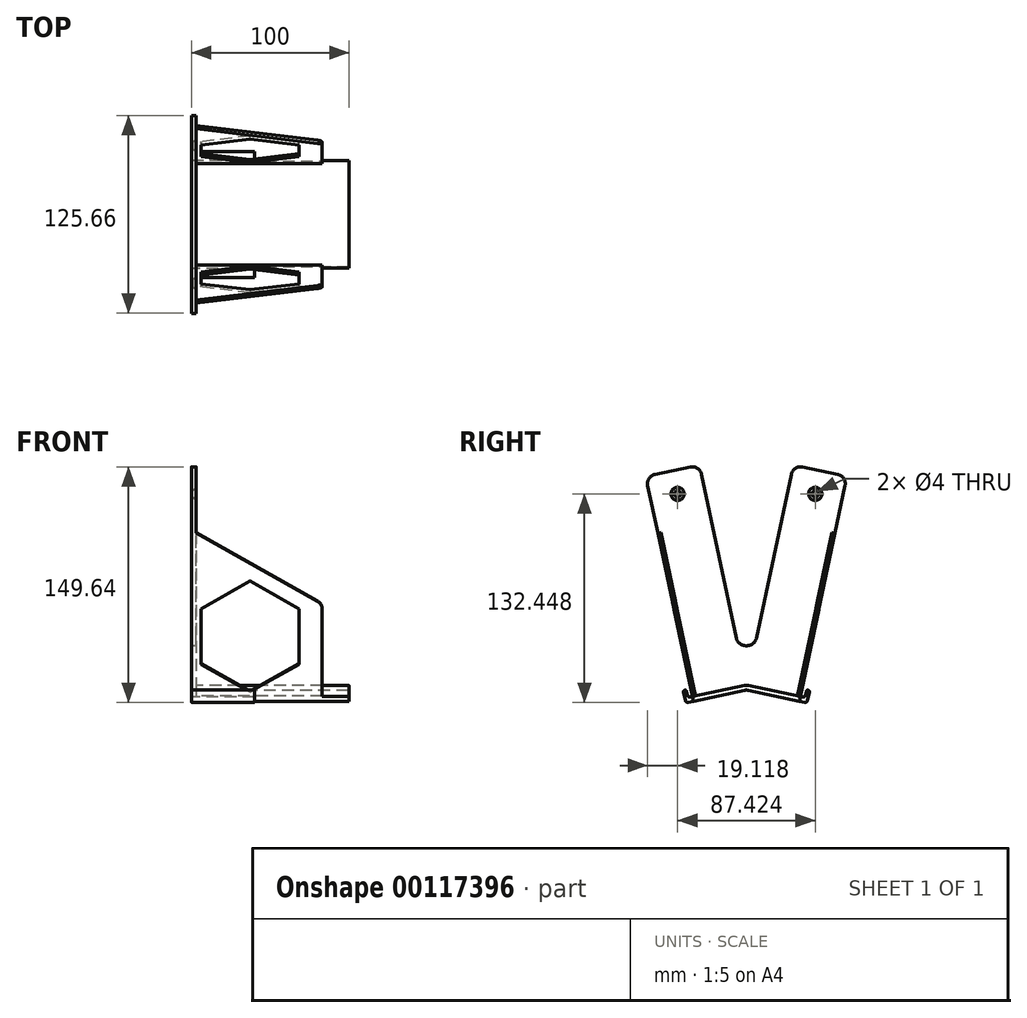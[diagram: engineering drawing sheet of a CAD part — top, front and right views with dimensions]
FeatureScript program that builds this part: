
annotation { "Feature Type Name" : "Feature", "Feature Type Description" : "" }
export const myFeature = defineFeature(function(context is Context, id is Id, definition is map)
    precondition{}
    {
        {
            var Q0;
            Q0=qCreatedBy(makeId("Right.planeOp"),FACE);
            var sketch = newSketch(context, id + "F0", { "sketchPlane" : qUnion([Q0])});
            skLineSegment(sketch, "E0", {"start": v(0, 0) * mm, "end": v(34.24, -7.28) * mm});
            skLineSegment(sketch, "E1", {"start": v(34.24, -7.28) * mm, "end": v(33.61, -10.21) * mm});
            skLineSegment(sketch, "E2", {"start": v(33.61, -10.21) * mm, "end": v(0, -3.07) * mm});
            skLineSegment(sketch, "E3", {"start": v(0, -3.07) * mm, "end": v(-33.61, -10.21) * mm});
            skLineSegment(sketch, "E4", {"start": v(-33.61, -10.21) * mm, "end": v(-34.24, -7.28) * mm});
            skLineSegment(sketch, "E5", {"start": v(-34.24, -7.28) * mm, "end": v(0, 0) * mm});
            skLineSegment(sketch, "E6", {"start": v(0, 0) * mm, "end": v(-5.31, 25) * mm});
            skLineSegment(sketch, "E7", {"start": v(-5.31, 25) * mm, "end": v(5.31, 25) * mm});
            skLineSegment(sketch, "E8", {"start": v(5.31, 25) * mm, "end": v(0, 0) * mm});
            skLineSegment(sketch, "E9", {"start": v(103.61, 139.79) * mm, "end": v(103.61, -10.21) * mm, "construction": true});
            skPoint(sketch, "E10", {"position": v(103.61, 64.79) * mm});
            skLineSegment(sketch, "E11", {"start": v(34.24, -7.28) * mm, "end": v(63.95, 132.51) * mm});
            skLineSegment(sketch, "E12", {"start": v(63.95, 132.51) * mm, "end": v(29.71, 139.79) * mm});
            skLineSegment(sketch, "E13", {"start": v(5.31, 25) * mm, "end": v(29.71, 139.79) * mm});
            skLineSegment(sketch, "E14", {"start": v(-34.24, -7.28) * mm, "end": v(-63.95, 132.51) * mm});
            skLineSegment(sketch, "E15", {"start": v(-63.95, 132.51) * mm, "end": v(-29.71, 139.79) * mm});
            skLineSegment(sketch, "E16", {"start": v(-29.71, 139.79) * mm, "end": v(-5.31, 25) * mm});
            skLineSegment(sketch, "E17", {"start": v(-34.24, -7.28) * mm, "end": v(-37.17, -7.9) * mm});
            skLineSegment(sketch, "E18", {"start": v(-37.17, -7.9) * mm, "end": v(-38.2, -3) * mm});
            skLineSegment(sketch, "E19", {"start": v(-38.2, -3) * mm, "end": v(-40.17, -3.43) * mm});
            skLineSegment(sketch, "E20", {"start": v(-40.17, -3.43) * mm, "end": v(-38.5, -11.25) * mm});
            skLineSegment(sketch, "E21", {"start": v(-38.5, -11.25) * mm, "end": v(-33.61, -10.21) * mm});
            skLineSegment(sketch, "E22", {"start": v(33.61, -10.21) * mm, "end": v(38.5, -11.25) * mm});
            skLineSegment(sketch, "E23", {"start": v(38.5, -11.25) * mm, "end": v(40.17, -3.43) * mm});
            skLineSegment(sketch, "E24", {"start": v(40.17, -3.43) * mm, "end": v(38.2, -3) * mm});
            skLineSegment(sketch, "E25", {"start": v(38.2, -3) * mm, "end": v(37.17, -7.9) * mm});
            skLineSegment(sketch, "E26", {"start": v(37.17, -7.9) * mm, "end": v(34.24, -7.28) * mm});
            skCircle(sketch, "E27", {"center": v(-43.71, 121.48) * mm, "radius": 2 * mm});
            skLineSegment(sketch, "E28", {"start": v(-46.83, 136.15) * mm, "end": v(-40.6, 106.8) * mm, "construction": true});
            skLineSegment(sketch, "E29", {"start": v(46.83, 136.15) * mm, "end": v(39.76, 102.9) * mm, "construction": true});
            skCircle(sketch, "E30", {"center": v(43.71, 121.48) * mm, "radius": 2 * mm});
            skSolve(sketch);
        }
        {
            var Q0;
            {var subQ6=sQuery(id+"F0.wireOp",EDGE,"E1");Q0=makeQuery(id+"F0.imprint","IMPRINT",FACE,{"disambiguationData":[TD([[makeQuery(id+"F0.imprint","IMPRINT",EDGE,{"derivedFrom":subQ6}),-1.0]])]});}
            extrude(context, id + "F1", {"entities" : qUnion([Q0]), "depth" : 100 * mm});
        }
        {
            var Q0;
            {var subQ1=sQuery(id+"F0.wireOp",EDGE,"E8");Q0=makeQuery(id+"F0.imprint","IMPRINT",FACE,{"disambiguationData":[TD([[makeQuery(id+"F0.imprint","IMPRINT",EDGE,{"derivedFrom":subQ1}),1.0]])]});}
            var Q1;
            {var subQ4=sQuery(id+"F0.wireOp",EDGE,"E6");Q1=makeQuery(id+"F0.imprint","IMPRINT",FACE,{"disambiguationData":[TD([[makeQuery(id+"F0.imprint","IMPRINT",EDGE,{"derivedFrom":subQ4}),-1.0]])]});}
            var Q2;
            {var subQ1=sQuery(id+"F0.wireOp",EDGE,"E6");Q2=makeQuery(id+"F0.imprint","IMPRINT",FACE,{"disambiguationData":[TD([[makeQuery(id+"F0.imprint","IMPRINT",EDGE,{"derivedFrom":subQ1}),1.0]])]});}
            extrude(context, id + "F2", {"entities" : qUnion([Q0, Q1, Q2]), "operationType" : NewBodyOperationType.ADD, "depth" : 3 * mm});
        }
        {
            var Q0;
            Q0=makeQuery(id+"F0.imprint","IMPRINT",FACE,{"disambiguationData":[TD([[makeQuery(id+"F0.imprint","IMPRINT",EDGE,{"derivedFrom":sQuery(id+"F0.wireOp",EDGE,"E4")}),1.0]])]});
            var Q1;
            Q1=makeQuery(id+"F0.imprint","IMPRINT",FACE,{"disambiguationData":[TD([[makeQuery(id+"F0.imprint","IMPRINT",EDGE,{"derivedFrom":sQuery(id+"F0.wireOp",EDGE,"E1")}),1.0]])]});
            extrude(context, id + "F3", {"entities" : qUnion([Q0, Q1]), "operationType" : NewBodyOperationType.ADD, "depth" : 40 * mm});
        }
        {
            var Q0;
            Q0=makeQuery(id+"F2.boolean.opBoolean","MERGE",FACE,{"derivedFrom":[makeQuery(id+"F1.opExtrude","SWEPT_FACE",FACE,{"disambiguationData":[OSD([sQuery(id+"F0.wireOp",EDGE,"E1")])]}),makeQuery(id+"F2.opExtrude","SWEPT_FACE",FACE,{"disambiguationData":[OSD([sQuery(id+"F0.wireOp",EDGE,"E11")])]})]});
            var sketch = newSketch(context, id + "F4", { "sketchPlane" : qUnion([Q0])});
            skLineSegment(sketch, "E31.top", {"start": v(-83, 60) * mm, "end": v(-3, 60) * mm});
            skLineSegment(sketch, "E31.left", {"start": v(-83, 0) * mm, "end": v(-83, 60) * mm});
            skLineSegment(sketch, "E31.right", {"start": v(-3, 0) * mm, "end": v(-3, 60) * mm});
            skLineSegment(sketch, "E32", {"start": v(-83, 60) * mm, "end": v(-3, 106.19) * mm});
            skLineSegment(sketch, "E33", {"start": v(-83, 0) * mm, "end": v(-3, 0) * mm});
            skLineSegment(sketch, "E34", {"start": v(-3, 106.19) * mm, "end": v(-3, 60) * mm});
            skSolve(sketch);
        }
        {
            var Q0;
            Q0=qSketchRegion(id+"F4",true);
            extrude(context, id + "F5", {"entities" : qUnion([Q0]), "oppositeDirection" : true, "depth" : 2 * mm});
        }
        {
            var Q0;
            Q0=makeQuery(id+"F5.boolean.opBoolean","MERGE",FACE,{"derivedFrom":[makeQuery(id+"F2.boolean.opBoolean","MERGE",FACE,{"derivedFrom":[makeQuery(id+"F1.opExtrude","SWEPT_FACE",FACE,{"disambiguationData":[OSD([sQuery(id+"F0.wireOp",EDGE,"E1")])]}),makeQuery(id+"F2.opExtrude","SWEPT_FACE",FACE,{"disambiguationData":[OSD([sQuery(id+"F0.wireOp",EDGE,"E11")])]})]}),makeQuery(id+"F5.opExtrude","CAP_FACE",FACE,{"disambiguationData":[OSD([sQuery(id+"F4.wireOp",EDGE,"E31.left"),sQuery(id+"F4.wireOp",EDGE,"E31.right"),sQuery(id+"F4.wireOp",EDGE,"E32"),sQuery(id+"F4.wireOp",EDGE,"E33"),sQuery(id+"F4.wireOp",EDGE,"E34")])],"isStart":true})]});
            var sketch = newSketch(context, id + "F6", { "sketchPlane" : qUnion([Q0])});
            skCircle(sketch, "E35.cCircle", {"center": v(-37.15, 38.96) * mm, "radius": 35.96 * mm, "construction": true});
            skLineSegment(sketch, "E35.0", {"start": v(-37.15, 3) * mm, "end": v(-68.3, 20.98) * mm});
            skLineSegment(sketch, "E35.1", {"start": v(-68.3, 20.98) * mm, "end": v(-68.3, 56.95) * mm});
            skLineSegment(sketch, "E35.2", {"start": v(-68.3, 56.95) * mm, "end": v(-37.15, 74.93) * mm});
            skLineSegment(sketch, "E35.3", {"start": v(-37.15, 74.93) * mm, "end": v(-6, 56.95) * mm});
            skLineSegment(sketch, "E35.4", {"start": v(-6, 56.95) * mm, "end": v(-6, 20.98) * mm});
            skLineSegment(sketch, "E35.5", {"start": v(-6, 20.98) * mm, "end": v(-37.15, 3) * mm});
            skSolve(sketch);
        }
        {
            var Q0;
            Q0=makeQuery(id+"F6.imprint","IMPRINT",FACE,{"disambiguationData":[TD([[makeQuery(id+"F6.imprint","IMPRINT",EDGE,{"derivedFrom":sQuery(id+"F6.wireOp",EDGE,"E35.0")}),-1.0]])]});
            extrude(context, id + "F7", {"entities" : qUnion([Q0]), "operationType" : NewBodyOperationType.REMOVE, "oppositeDirection" : true, "depth" : 25 * mm});
        }
        {
            var Q0;
            Q0=makeQuery(id+"F5.opExtrude","SWEPT_BODY",BODY,{"disambiguationData":[OSD([sQuery(id+"F4.wireOp",EDGE,"E31.left"),sQuery(id+"F4.wireOp",EDGE,"E31.right"),sQuery(id+"F4.wireOp",EDGE,"E32"),sQuery(id+"F4.wireOp",EDGE,"E33"),sQuery(id+"F4.wireOp",EDGE,"E34")])]});
            var Q1;
            Q1=qCreatedBy(makeId("Front.planeOp"),FACE);
            mirror(context, id + "F8", {"operationType" : NewBodyOperationType.ADD, "entities" : qUnion([Q0]), "mirrorPlane" : qUnion([Q1])});
        }
        {
            var Q0;
            Q0=makeQuery(id+"F8.opPattern","COPY",EDGE,{"derivedFrom":makeQuery(id+"F5.opExtrude","SWEPT_EDGE",EDGE,{"disambiguationData":[OSD([sQuery(id+"F0.wireOp",EDGE,"E11"),sQuery(id+"F4.wireOp",EDGE,"E32"),sQuery(id+"F4.wireOp",EDGE,"E34")])]}),"instanceName":"1"});
            var Q1;
            Q1=makeQuery(id+"F5.opExtrude","SWEPT_EDGE",EDGE,{"disambiguationData":[OSD([sQuery(id+"F0.wireOp",EDGE,"E11"),sQuery(id+"F4.wireOp",EDGE,"E32"),sQuery(id+"F4.wireOp",EDGE,"E34")])]});
            var Q2;
            Q2=makeQuery(id+"F8.opPattern","COPY",EDGE,{"derivedFrom":makeQuery(id+"F5.opExtrude","SWEPT_EDGE",EDGE,{"disambiguationData":[OSD([sQuery(id+"F4.wireOp",EDGE,"E31.top"),sQuery(id+"F4.wireOp",EDGE,"E31.left"),sQuery(id+"F4.wireOp",EDGE,"E32")])]}),"instanceName":"1"});
            var Q3;
            Q3=makeQuery(id+"F5.opExtrude","SWEPT_EDGE",EDGE,{"disambiguationData":[OSD([sQuery(id+"F4.wireOp",EDGE,"E31.top"),sQuery(id+"F4.wireOp",EDGE,"E31.left"),sQuery(id+"F4.wireOp",EDGE,"E32")])]});
            var Q4;
            Q4=makeQuery(id+"F8.opPattern","COPY",EDGE,{"derivedFrom":makeQuery(id+"F5.opExtrude","SWEPT_EDGE",EDGE,{"disambiguationData":[OSD([sQuery(id+"F0.wireOp",EDGE,"E0"),sQuery(id+"F0.wireOp",EDGE,"E1"),sQuery(id+"F0.wireOp",EDGE,"E11"),sQuery(id+"F4.wireOp",EDGE,"E31.left"),sQuery(id+"F4.wireOp",EDGE,"E33")])]}),"instanceName":"1"});
            var Q5;
            Q5=makeQuery(id+"F5.opExtrude","SWEPT_EDGE",EDGE,{"disambiguationData":[OSD([sQuery(id+"F0.wireOp",EDGE,"E0"),sQuery(id+"F0.wireOp",EDGE,"E1"),sQuery(id+"F0.wireOp",EDGE,"E11"),sQuery(id+"F4.wireOp",EDGE,"E31.left"),sQuery(id+"F4.wireOp",EDGE,"E33")])]});
            var Q6;
            Q6=makeQuery(id+"F2.opExtrude","SWEPT_EDGE",EDGE,{"disambiguationData":[OSD([sQuery(id+"F0.wireOp",EDGE,"E6"),sQuery(id+"F0.wireOp",EDGE,"E7"),sQuery(id+"F0.wireOp",EDGE,"E16")])]});
            var Q7;
            Q7=makeQuery(id+"F2.opExtrude","SWEPT_EDGE",EDGE,{"disambiguationData":[OSD([sQuery(id+"F0.wireOp",EDGE,"E7"),sQuery(id+"F0.wireOp",EDGE,"E8"),sQuery(id+"F0.wireOp",EDGE,"E13")])]});
            var Q8;
            Q8=makeQuery(id+"F1.opExtrude","SWEPT_EDGE",EDGE,{"disambiguationData":[OSD([sQuery(id+"F0.wireOp",EDGE,"E0"),sQuery(id+"F0.wireOp",EDGE,"E5")])]});
            var Q9;
            Q9=makeQuery(id+"F1.opExtrude","SWEPT_EDGE",EDGE,{"disambiguationData":[OSD([sQuery(id+"F0.wireOp",EDGE,"E2"),sQuery(id+"F0.wireOp",EDGE,"E3")])]});
            var Q10;
            Q10=makeQuery(id+"F2.opExtrude","SWEPT_EDGE",EDGE,{"disambiguationData":[OSD([sQuery(id+"F0.wireOp",EDGE,"E15"),sQuery(id+"F0.wireOp",EDGE,"E16")])]});
            var Q11;
            Q11=makeQuery(id+"F2.opExtrude","SWEPT_EDGE",EDGE,{"disambiguationData":[OSD([sQuery(id+"F0.wireOp",EDGE,"E14"),sQuery(id+"F0.wireOp",EDGE,"E15")])]});
            var Q12;
            Q12=makeQuery(id+"F2.opExtrude","SWEPT_EDGE",EDGE,{"disambiguationData":[OSD([sQuery(id+"F0.wireOp",EDGE,"E12"),sQuery(id+"F0.wireOp",EDGE,"E13")])]});
            var Q13;
            Q13=makeQuery(id+"F2.opExtrude","SWEPT_EDGE",EDGE,{"disambiguationData":[OSD([sQuery(id+"F0.wireOp",EDGE,"E11"),sQuery(id+"F0.wireOp",EDGE,"E12")])]});
            fillet(context, id + "F9", {"entities" : qUnion([Q0, Q1, Q2, Q3, Q4, Q5, Q6, Q7, Q8, Q9, Q10, Q11, Q12, Q13]), "radius" : 6 * mm, "tangentPropagation" : true, "allowEdgeOverflow" : false});
        }
        {
            var Q0;
            Q0=makeQuery(id+"F8.boolean.opBoolean","MERGE",EDGE,{"derivedFrom":[makeQuery(id+"F3.opExtrude","SWEPT_EDGE",EDGE,{"disambiguationData":[OSD([sQuery(id+"F0.wireOp",EDGE,"E0"),sQuery(id+"F0.wireOp",EDGE,"E1"),sQuery(id+"F0.wireOp",EDGE,"E11"),sQuery(id+"F0.wireOp",EDGE,"E26")])]}),makeQuery(id+"F5.opExtrude","CAP_EDGE",EDGE,{"disambiguationData":[OSD([sQuery(id+"F4.wireOp",EDGE,"E33")])],"isStart":true})]});
            var Q1;
            Q1=makeQuery(id+"F3.opExtrude","SWEPT_EDGE",EDGE,{"disambiguationData":[OSD([sQuery(id+"F0.wireOp",EDGE,"E25"),sQuery(id+"F0.wireOp",EDGE,"E26")])]});
            var Q2;
            Q2=makeQuery(id+"F3.opExtrude","SWEPT_EDGE",EDGE,{"disambiguationData":[OSD([sQuery(id+"F0.wireOp",EDGE,"E17"),sQuery(id+"F0.wireOp",EDGE,"E18")])]});
            var Q3;
            Q3=makeQuery(id+"F8.boolean.opBoolean","MERGE",EDGE,{"derivedFrom":[makeQuery(id+"F3.opExtrude","SWEPT_EDGE",EDGE,{"disambiguationData":[OSD([sQuery(id+"F0.wireOp",EDGE,"E4"),sQuery(id+"F0.wireOp",EDGE,"E5"),sQuery(id+"F0.wireOp",EDGE,"E14"),sQuery(id+"F0.wireOp",EDGE,"E17")])]}),makeQuery(id+"F8.opPattern","COPY",EDGE,{"derivedFrom":makeQuery(id+"F5.opExtrude","CAP_EDGE",EDGE,{"disambiguationData":[OSD([sQuery(id+"F4.wireOp",EDGE,"E33")])],"isStart":true}),"instanceName":"1"})]});
            var Q4;
            Q4=makeQuery(id+"F3.opExtrude","SWEPT_EDGE",EDGE,{"disambiguationData":[OSD([sQuery(id+"F0.wireOp",EDGE,"E20"),sQuery(id+"F0.wireOp",EDGE,"E21")])]});
            var Q5;
            Q5=makeQuery(id+"F3.opExtrude","SWEPT_EDGE",EDGE,{"disambiguationData":[OSD([sQuery(id+"F0.wireOp",EDGE,"E22"),sQuery(id+"F0.wireOp",EDGE,"E23")])]});
            fillet(context, id + "F10", {"entities" : qUnion([Q0, Q1, Q2, Q3, Q4, Q5]), "radius" : 1.5 * mm, "allowEdgeOverflow" : false});
        }
        {
            var Q0;
            Q0=makeQuery(id+"F3.opExtrude","SWEPT_EDGE",EDGE,{"disambiguationData":[OSD([sQuery(id+"F0.wireOp",EDGE,"E23"),sQuery(id+"F0.wireOp",EDGE,"E24")])]});
            var Q1;
            Q1=makeQuery(id+"F3.opExtrude","SWEPT_EDGE",EDGE,{"disambiguationData":[OSD([sQuery(id+"F0.wireOp",EDGE,"E24"),sQuery(id+"F0.wireOp",EDGE,"E25")])]});
            var Q2;
            Q2=makeQuery(id+"F3.opExtrude","SWEPT_EDGE",EDGE,{"disambiguationData":[OSD([sQuery(id+"F0.wireOp",EDGE,"E19"),sQuery(id+"F0.wireOp",EDGE,"E20")])]});
            var Q3;
            Q3=makeQuery(id+"F3.opExtrude","SWEPT_EDGE",EDGE,{"disambiguationData":[OSD([sQuery(id+"F0.wireOp",EDGE,"E18"),sQuery(id+"F0.wireOp",EDGE,"E19")])]});
            fillet(context, id + "F11", {"entities" : qUnion([Q0, Q1, Q2, Q3]), "radius" : 1 * mm, "allowEdgeOverflow" : false});
        }
        {
            var Q0;
            Q0=makeQuery(id+"F2.opExtrude","CAP_EDGE",EDGE,{"disambiguationData":[OSD([sQuery(id+"F0.wireOp",EDGE,"E27")])],"isStart":false});
            var Q1;
            Q1=makeQuery(id+"F2.opExtrude","CAP_EDGE",EDGE,{"disambiguationData":[OSD([sQuery(id+"F0.wireOp",EDGE,"E30")])],"isStart":false});
            chamfer(context, id + "F12", {"entities" : qUnion([Q0, Q1]), "width" : 2.2 * mm, "tangentPropagation" : true});
        }
    });
